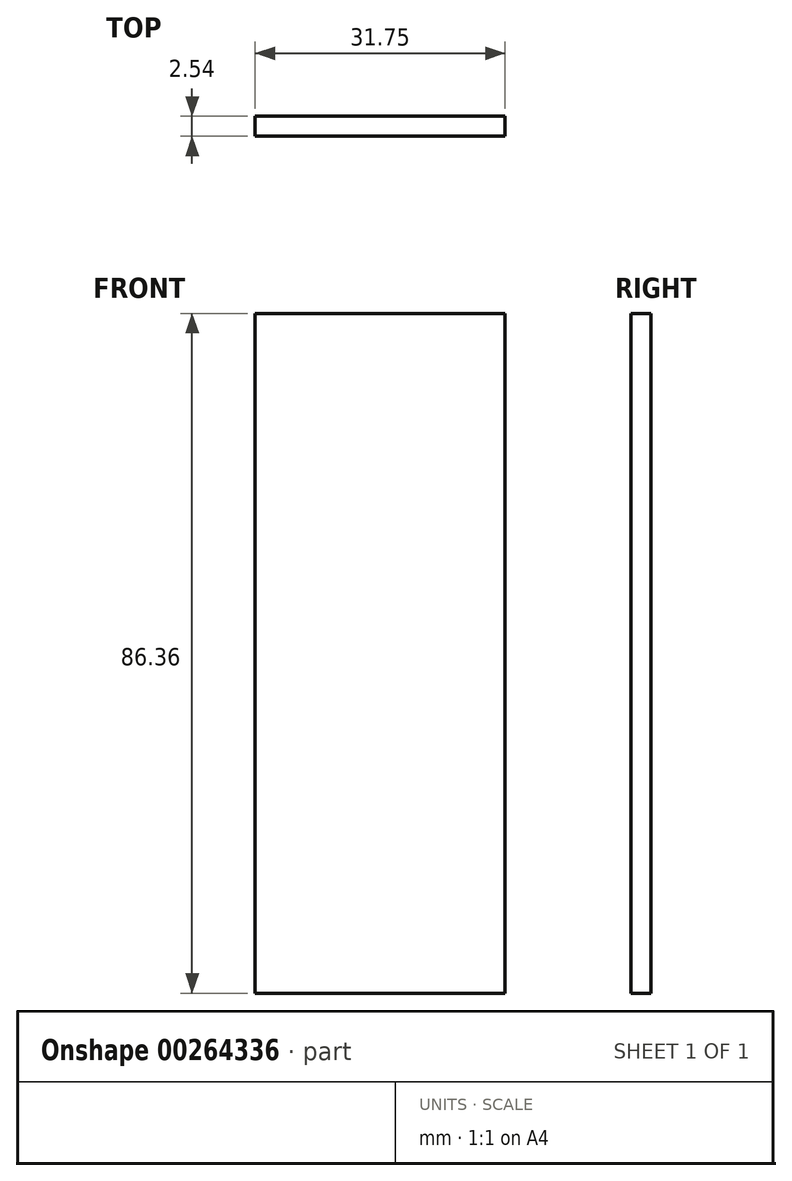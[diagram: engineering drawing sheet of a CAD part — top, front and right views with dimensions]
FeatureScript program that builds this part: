
annotation { "Feature Type Name" : "Feature", "Feature Type Description" : "" }
export const myFeature = defineFeature(function(context is Context, id is Id, definition is map)
    precondition{}
    {
        {
            var Q0;
            Q0=qCreatedBy(makeId("Front.planeOp"),FACE);
            var sketch = newSketch(context, id + "F0", { "sketchPlane" : qUnion([Q0])});
            skLineSegment(sketch, "E0.bottom", {"start": v(0, 0) * mm, "end": v(-31.75, 0) * mm});
            skLineSegment(sketch, "E0.top", {"start": v(0, 86.36) * mm, "end": v(-31.75, 86.36) * mm});
            skLineSegment(sketch, "E0.left", {"start": v(0, 0) * mm, "end": v(0, 86.36) * mm});
            skLineSegment(sketch, "E0.right", {"start": v(-31.75, 0) * mm, "end": v(-31.75, 86.36) * mm});
            skSolve(sketch);
        }
        {
            var Q0;
            Q0=makeQuery(id+"F0.imprint","IMPRINT",FACE,{"disambiguationData":[TD([[makeQuery(id+"F0.imprint","IMPRINT",EDGE,{"derivedFrom":sQuery(id+"F0.wireOp",EDGE,"E0.bottom")}),-1.0]])]});
            extrude(context, id + "F1", {"entities" : qUnion([Q0]), "depth" : 2.54 * mm});
        }
    });
